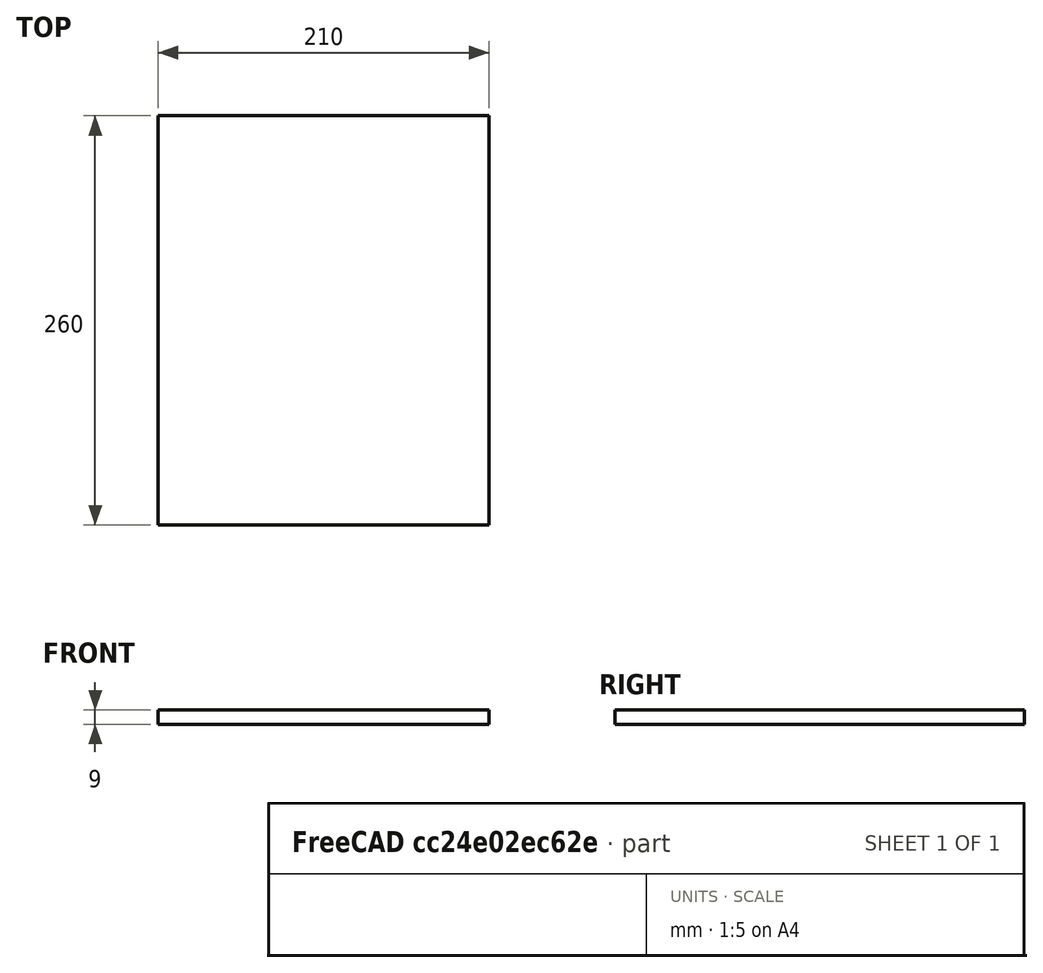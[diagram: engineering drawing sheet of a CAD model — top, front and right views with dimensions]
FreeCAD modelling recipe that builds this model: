
FCSTD DOCUMENT  (FreeCAD 0.16RUnknown)
Label: plaque_haut
License: All rights reserved
LicenseURL: http://en.wikipedia.org/wiki/All_rights_reserved
objects: App::FeaturePython×2, Drawing::FeatureViewPart×2, Part::Plane×1, Part::FeaturePython×1, Part::Extrusion×1, App::DocumentObjectGroup×1, Drawing::FeatureViewPython×1, Drawing::FeaturePage×1
note: 3 computed .brp shape members not serialized (recipe doc carries the construction recipe); baked Part::Feature solids carry a one-line shape summary decoded from their .brp

FEATURE [Part::Plane] square
  Length = 210
  Placement = pos=(0,-130,0) rot=(0,0,1;0rad)
  Width = 260
FEATURE [Part::FeaturePython] RefineLinearExtrude  # WARN: FeaturePython — macro-defined, semantics opaque (R4)
  Base = -> square
FEATURE [Part::Extrusion] LinearExtrude
  Base = -> RefineLinearExtrude
  Dir = (0,0,9)
  Solid = true
FEATURE [App::FeaturePython] Dimension  # Draft dimension (typed FeaturePython)
  Dimline = (0,136,0)
  Direction = (0,0,0)
  Distance = 210
  End = (210,130,0)
  Normal = (0,0,1)
  Start = (0,130,0)
FEATURE [Drawing::FeatureViewPart] Ortho002  label="Ortho_1_-1"
  Direction = (0.57735,-0.57735,0.57735)
  HiddenWidth = 0.15
  LineWidth = 0.35
  Rotation = 60
  Scale = 0.5
  ShowHiddenLines = false
  ShowSmoothLines = false
  Source = -> LinearExtrude
  Tolerance = 0.05
  ViewResult = <g id="Ortho_1_-1"\n   transform="rotate(60,278.294,111.071) translate(278.294,111.071) scale(0.5,0.5)"\n  >\n<g   stroke="rgb(0, 0, 0)"\n   stroke-width="0.7"\n   stroke-linecap="butt"\n   stroke-linejoin="miter"\n   fill="none"\n   transform="scale(1,-1)"\n  >\n<path id= "1" d=" M 0 -106.145 L -6.36396 -102.47 " />\n<path id= "2" d=" M -6.36396 -102.47 L -6.36396 109.819 " />\n<path id= "3" d=" M 148.492 -20.4124 L 142.128 -16.7382 " />\n<path id= "4" d=" M 0 -106.145 L 148.492 -20.4124 " />\n<path id= "5" d=" M -6.36396 -102.47 L 142.128 -16.7382 " />\n<path id= "6" d=" M 148.492 191.877 L 142.128 195.551 " />\n<path id= "7" d=" M 148.492 -20.4124 L 148.492 191.877 " />\n<path id= "8" d=" M 142.128 -16.7382 L 142.128 195.551 " />\n<path id= "9" d=" M -6.36396 109.819 L 142.128 195.551 " />\n</g>\n</g>
  Visible = true
  X = 278.294
  Y = 111.071
FEATURE [Drawing::FeatureViewPart] Ortho003  label="Ortho_0_-1"
  Direction = (0,0,1)
  HiddenWidth = 0.15
  LineWidth = 0.35
  Rotation = 90
  Scale = 0.5
  ShowHiddenLines = false
  ShowSmoothLines = false
  Source = -> LinearExtrude
  Tolerance = 0.05
  ViewResult = <g id="Ortho_0_-1"\n   transform="rotate(90,123,75) translate(123,75) scale(0.5,0.5)"\n  >\n<g   stroke="rgb(0, 0, 0)"\n   stroke-width="0.7"\n   stroke-linecap="butt"\n   stroke-linejoin="miter"\n   fill="none"\n   transform="scale(1,-1)"\n  >\n<path id= "1" d=" M 0 -130 L 0 130 " />\n<path id= "2" d=" M 0 -130 L 210 -130 " />\n<path id= "3" d=" M 210 -130 L 210 130 " />\n<path id= "4" d=" M 0 130 L 210 130 " />\n</g>\n</g>
  Visible = true
  X = 123
  Y = 75
FEATURE [App::FeaturePython] Dimension002  # Draft dimension (typed FeaturePython)
  Dimline = (-6,0,0)
  Direction = (0,0,0)
  Distance = 260
  End = (0,130,0)
  Normal = (0,0,1)
  Start = (0,-130,0)
FEATURE [App::DocumentObjectGroup] Groupe  label="Dimensions XY"
  Group = -> [Dimension,Dimension002]
FEATURE [Drawing::FeatureViewPython] ViewGroupe  # drawing view (typed FeaturePython)
  Direction = (0,0,0)
  FillStyle = 0
  FontSize = 12
  LineStyle = 0
  LineWidth = 0.35
  Rotation = 90
  Scale = 0.5
  Source = -> Groupe
  ViewResult = <g id="ViewGroupe" transform="rotate(90.0,123.0,75.0) translate(123.0,75.0) scale(0.5,-0.5)"><path d="M 0.0 130.0 L 0.0 136.0 L 210.0 136.0 L 210.0 130.0" fill="none" stroke="#000000" stroke-width="0.7 px" style="stroke-width:0.7;stroke-miterlimit:4;stroke-dasharray:none" freecad:basepoint1="0.0 130.0" freecad:basepoint2="210.0 130.0" freecad:dimpoint="0.0 136.0"/>\n<path transform="rotate(-0.0,0.0,136.0) translate(0.0,136.0) scale(0.666666666667,0.666666666667)" freecad:skip="1" fill="#000000" stroke="none" style="stroke-miterlimit:4;stroke-dasharray:none" d="M 0 0 L 4 1 L 4 -1 Z"/>\n<path transform="rotate(180.0,210.0,136.0) translate(210.0,136.0) scale(0.666666666667,0.666666666667)" freecad:skip="1" fill="#000000" stroke="none" style="stroke-miterlimit:4;stroke-dasharray:none" d="M 0 0 L 4 1 L 4 -1 Z"/>\n<text fill="#000000" font-size="12.0" style="text-anchor:middle;text-align:center;font-family:" transform="rotate(-0.0,105.0,137.0) translate(105.0,137.0) scale(1,-1) " freecad:skip="1">\n210,00 </text>\n<path d="M 0.0 -130.0 L -6.0 -130.0 L -6.0 130.0 L 0.0 130.0" fill="none" stroke="#000000" stroke-width="0.7 px" style="stroke-width:0.7;stroke-miterlimit:4;stroke-dasharray:none" freecad:basepoint1="0.0 -130.0" freecad:basepoint2="0.0 130.0" freecad:dimpoint="-6.0 -130.0"/>\n<path transform="rotate(90.0,-6.0,-130.0) translate(-6.0,-130.0) scale(0.666666666667,0.666666666667)" freecad:skip="1" fill="#000000" stroke="none" style="stroke-miterlimit:4;stroke-dasharray:none" d="M 0 0 L 4 1 L 4 -1 Z"/>\n<path transform="rotate(270.0,-6.0,130.0) translate(-6.0,130.0) scale(0.666666666667,0.666666666667)" freecad:skip="1" fill="#000000" stroke="none" style="stroke-miterlimit:4;stroke-dasharray:none" d="M 0 0 L 4 1 L 4 -1 Z"/>\n<text fill="#000000" font-size="12.0" style="text-anchor:middle;text-align:center;font-family:" transform="rotate(90.0,-7.0,0.0) translate(-7.0,0.0) scale(1,-1) " freecad:skip="1">\n260,00 </text>\n</g>
  Visible = true
  X = 123
  Y = 75
FEATURE [Drawing::FeaturePage] Page
  EditableTexts = AUTHOR NAME | CREATION DATE | SUPERVISOR NAME | CHECK DATE | 0,5 | WEIGHT | NUMBER | SHEET | Caisse | Haut
  Group = -> [ViewGroupe,Ortho002,Ortho003]
